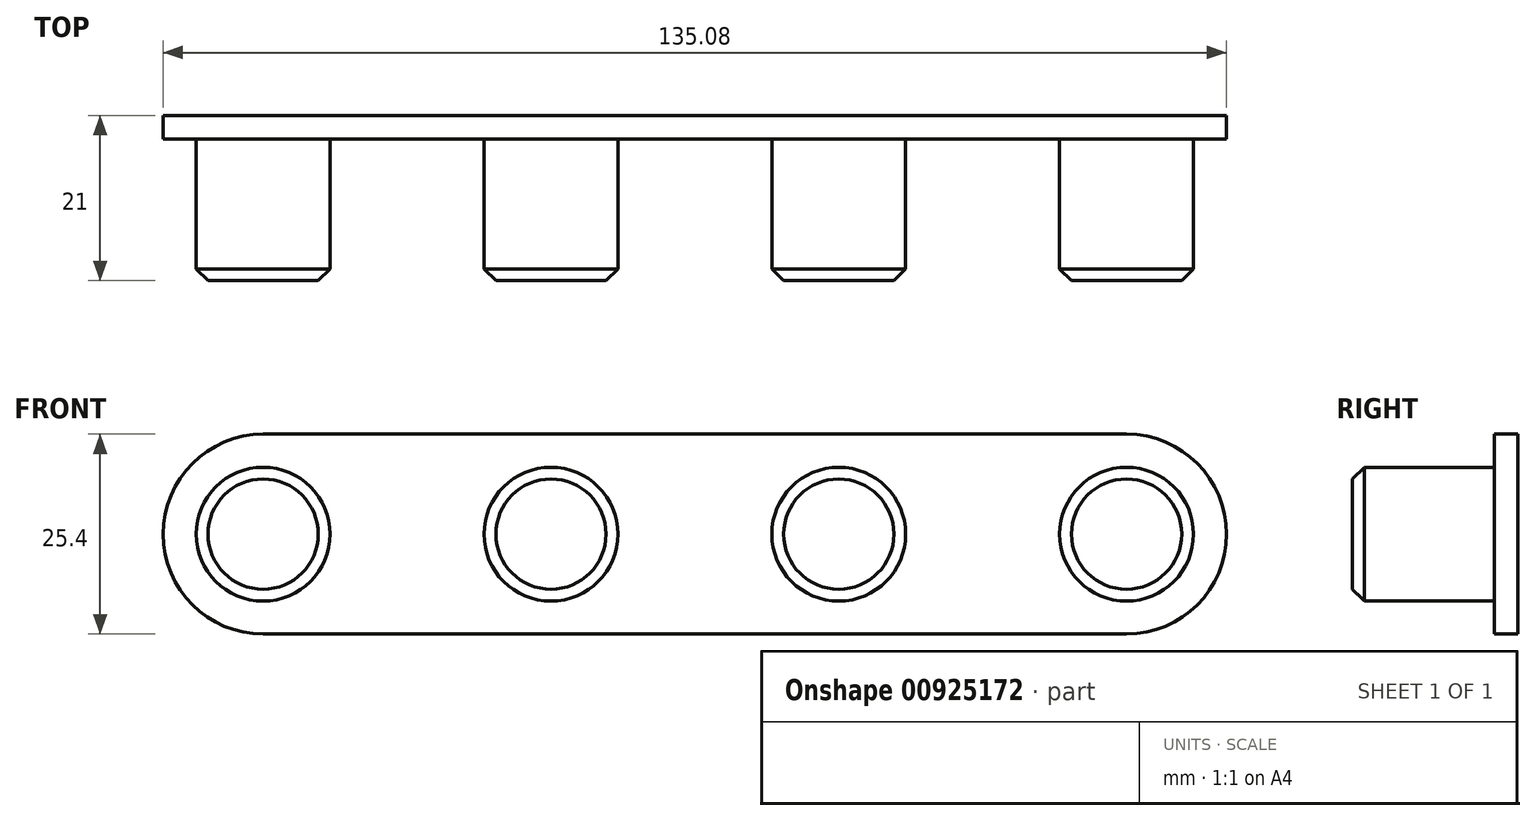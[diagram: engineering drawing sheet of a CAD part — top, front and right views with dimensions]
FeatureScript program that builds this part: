
annotation { "Feature Type Name" : "Feature", "Feature Type Description" : "" }
export const myFeature = defineFeature(function(context is Context, id is Id, definition is map)
    precondition{}
    {
        {
            var Q0;
            Q0=qCreatedBy(makeId("Front.planeOp"),FACE);
            var sketch = newSketch(context, id + "F0", { "sketchPlane" : qUnion([Q0])});
            skLineSegment(sketch, "E0.bottom", {"start": v(-54.84, 12.7) * mm, "end": v(54.84, 12.7) * mm});
            skLineSegment(sketch, "E0.top", {"start": v(-54.84, -12.7) * mm, "end": v(54.84, -12.7) * mm});
            skLineSegment(sketch, "E0.left", {"start": v(-67.54, 0) * mm, "end": v(-67.54, 0) * mm});
            skLineSegment(sketch, "E0.right", {"start": v(67.54, 0) * mm, "end": v(67.54, 0) * mm});
            skPoint(sketch, "E1.visualSharp", {"position": v(-67.54, 12.7) * mm});
            skArc(sketch, "E1.filletArc", {"start": v(-54.84, 12.7) * mm, "mid": v(-63.82, 8.98) * mm, "end": v(-67.54, 0) * mm});
            skPoint(sketch, "E2.visualSharp", {"position": v(-67.54, -12.7) * mm});
            skArc(sketch, "E2.filletArc", {"start": v(-67.54, 0) * mm, "mid": v(-63.82, -8.98) * mm, "end": v(-54.84, -12.7) * mm});
            skPoint(sketch, "E3.visualSharp", {"position": v(67.54, -12.7) * mm});
            skArc(sketch, "E3.filletArc", {"start": v(54.84, -12.7) * mm, "mid": v(63.82, -8.98) * mm, "end": v(67.54, 0) * mm});
            skPoint(sketch, "E4.visualSharp", {"position": v(67.54, 12.7) * mm});
            skArc(sketch, "E4.filletArc", {"start": v(67.54, 0) * mm, "mid": v(63.82, 8.98) * mm, "end": v(54.84, 12.7) * mm});
            skSolve(sketch);
        }
        {
            var Q0;
            Q0 = qSketchRegion(id + "F0", true);
            extrude(context, id + "F1", {"entities" : qUnion([Q0]), "depth" : 3 * mm, "offsetDistance" : 25 * mm});
        }
        {
            var Q0;
            Q0=makeQuery(id+"F1.opExtrude","CAP_FACE",FACE,{"disambiguationData":[OSD([sQuery(id+"F0.wireOp",EDGE,"E0.bottom"),sQuery(id+"F0.wireOp",EDGE,"E0.top"),sQuery(id+"F0.wireOp",EDGE,"E1.filletArc"),sQuery(id+"F0.wireOp",EDGE,"E2.filletArc"),sQuery(id+"F0.wireOp",EDGE,"E3.filletArc"),sQuery(id+"F0.wireOp",EDGE,"E4.filletArc")])],"isStart":false});
            var sketch = newSketch(context, id + "F2", { "sketchPlane" : qUnion([Q0])});
            skCircle(sketch, "E5", {"center": v(-54.84, 0) * mm, "radius": 8.5 * mm});
            skCircle(sketch, "E6", {"center": v(54.84, 0) * mm, "radius": 8.5 * mm});
            skCircle(sketch, "E7", {"center": v(-18.28, 0) * mm, "radius": 8.5 * mm});
            skCircle(sketch, "E8", {"center": v(18.28, 0) * mm, "radius": 8.5 * mm});
            skSolve(sketch);
        }
        {
            var Q0;
            Q0 = qSketchRegion(id + "F2", true);
            extrude(context, id + "F3", {"entities" : qUnion([Q0]), "operationType" : NewBodyOperationType.ADD, "depth" : 18 * mm, "offsetDistance" : 25 * mm});
        }
        {
            var Q0;
            Q0=makeQuery(id+"F3.opExtrude","CAP_EDGE",EDGE,{"disambiguationData":[OSD([sQuery(id+"F2.wireOp",EDGE,"E5")])],"isStart":false});
            var Q1;
            Q1=makeQuery(id+"F3.opExtrude","CAP_EDGE",EDGE,{"disambiguationData":[OSD([sQuery(id+"F2.wireOp",EDGE,"E7")])],"isStart":false});
            var Q2;
            Q2=makeQuery(id+"F3.opExtrude","CAP_EDGE",EDGE,{"disambiguationData":[OSD([sQuery(id+"F2.wireOp",EDGE,"E8")])],"isStart":false});
            var Q3;
            Q3=makeQuery(id+"F3.opExtrude","CAP_EDGE",EDGE,{"disambiguationData":[OSD([sQuery(id+"F2.wireOp",EDGE,"E6")])],"isStart":false});
            var Q4;
            Q4=makeQuery(id+"F3.opExtrude","CAP_EDGE",EDGE,{"disambiguationData":[OSD([sQuery(id+"F2.wireOp",EDGE,"E7")])],"isStart":true});
            var Q5;
            Q5=makeQuery(id+"F3.opExtrude","CAP_EDGE",EDGE,{"disambiguationData":[OSD([sQuery(id+"F2.wireOp",EDGE,"E5")])],"isStart":true});
            var Q6;
            Q6=makeQuery(id+"F3.opExtrude","CAP_EDGE",EDGE,{"disambiguationData":[OSD([sQuery(id+"F2.wireOp",EDGE,"E8")])],"isStart":true});
            var Q7;
            Q7=makeQuery(id+"F3.opExtrude","CAP_EDGE",EDGE,{"disambiguationData":[OSD([sQuery(id+"F2.wireOp",EDGE,"E6")])],"isStart":true});
            chamfer(context, id + "F4", {"entities" : qUnion([Q0, Q1, Q2, Q3, Q4, Q5, Q6, Q7]), "width" : 1.5 * mm, "tangentPropagation" : true});
        }
    });
